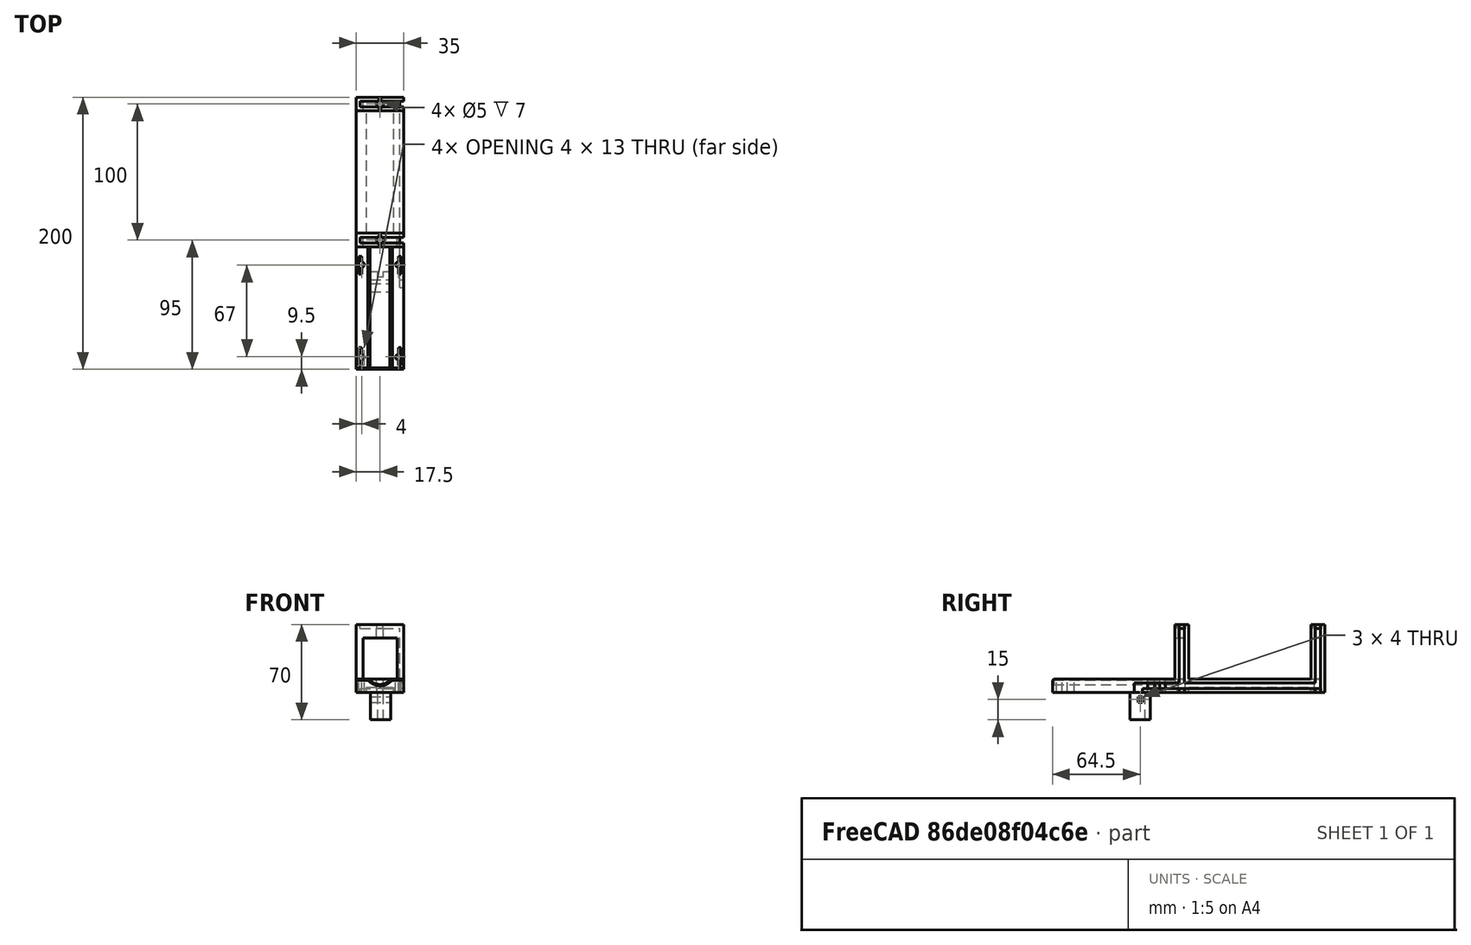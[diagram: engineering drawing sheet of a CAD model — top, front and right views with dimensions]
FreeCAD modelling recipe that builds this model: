
FCSTD DOCUMENT  (FreeCAD 0.19RUnknown)
Label: montaje_02
License: All rights reserved
LicenseURL: http://en.wikipedia.org/wiki/All_rights_reserved
objects: Part::Cut×38, Part::Box×20, Part::Cylinder×11, Part::Chamfer×1, Part::MultiFuse×1
note: 71 computed .brp shape members not serialized (recipe doc carries the construction recipe); baked Part::Feature solids carry a one-line shape summary decoded from their .brp

FEATURE [Part::Box] Box  label="Cubo"
  AttacherType = Attacher::AttachEngine3D
  Height = 10
  Length = 35
  Width = 200
FEATURE [Part::Box] Box001  label="Cubo001"
  AttacherType = Attacher::AttachEngine3D
  Height = 50
  Length = 35
  Placement = pos=(0,90,0) rot=(0,0,1;0rad)
  Width = 10
FEATURE [Part::Box] Box002  label="Cubo002"
  AttacherType = Attacher::AttachEngine3D
  Height = 50
  Length = 35
  Placement = pos=(0,190,0) rot=(0,0,1;0rad)
  Width = 10
FEATURE [Part::Cylinder] Cylinder  label="Cilindro"
  Angle = 360
  AttacherType = Attacher::AttachEngine3D
  Height = 90
  Placement = pos=(17.5,0,16) rot=(-1,0,0;1.5708rad)
  Radius = 10
FEATURE [Part::Cut] Cut
  Base = -> Box
  Tool = -> Cylinder
FEATURE [Part::Chamfer] Chamfer
  Base = -> Cut
  Edges = 5 edges r=1: [Edge6,Edge7,Edge8,Edge12,Edge14]
FEATURE [Part::Box] Box003  label="Cubo003"
  AttacherType = Attacher::AttachEngine3D
  Height = 30
  Length = 25
  Placement = pos=(5,0,10) rot=(0,0,1;0rad)
  Width = 220
FEATURE [Part::Cut] Cut001
  Base = -> Box001
  Tool = -> Box003
FEATURE [Part::Cut] Cut002
  Base = -> Box002
  Tool = -> Box003
FEATURE [Part::Box] Box004  label="Cubo004"
  AttacherType = Attacher::AttachEngine3D
  Height = 4
  Length = 3
  Placement = pos=(32,60,3) rot=(0,0,1;0rad)
  Width = 136
FEATURE [Part::Cut] Cut003
  Base = -> Chamfer
  Tool = -> Box004
FEATURE [Part::Cut] Cut004
  Base = -> Cut001
  Tool = -> Box004
FEATURE [Part::Cut] Cut005
  Base = -> Cut002
  Tool = -> Box004
FEATURE [Part::Box] Box005  label="Cubo005"
  AttacherType = Attacher::AttachEngine3D
  Height = 50
  Length = 3
  Placement = pos=(32,93,0) rot=(0,0,1;0rad)
  Width = 4
FEATURE [Part::Box] Box006  label="Cubo006"
  AttacherType = Attacher::AttachEngine3D
  Height = 50
  Length = 3
  Placement = pos=(32,193,0) rot=(0,0,1;0rad)
  Width = 4
FEATURE [Part::Cut] Cut006
  Base = -> Cut004
  Tool = -> Box005
FEATURE [Part::Cut] Cut007
  Base = -> Cut005
  Tool = -> Box006
FEATURE [Part::Cut] Cut008
  Base = -> Cut003
  Tool = -> Box005
FEATURE [Part::Cut] Cut009
  Base = -> Cut008
  Tool = -> Box006
FEATURE [Part::Box] Box007  label="Cubo007"
  AttacherType = Attacher::AttachEngine3D
  Height = 3
  Length = 30
  Placement = pos=(3,93,0) rot=(0,0,1;0rad)
  Width = 4
FEATURE [Part::Box] Box008  label="Cubo008"
  AttacherType = Attacher::AttachEngine3D
  Height = 3
  Length = 30
  Placement = pos=(3,193,0) rot=(0,0,1;0rad)
  Width = 4
FEATURE [Part::Cut] Cut010
  Base = -> Cut006
  Tool = -> Box007
FEATURE [Part::Cut] Cut011
  Base = -> Cut007
  Tool = -> Box008
FEATURE [Part::Cut] Cut012
  Base = -> Cut009
  Tool = -> Box007
FEATURE [Part::Cut] Cut013
  Base = -> Cut012
  Tool = -> Box008
FEATURE [Part::Box] Box009  label="Cubo009"
  AttacherType = Attacher::AttachEngine3D
  Height = 3
  Length = 30
  Placement = pos=(3,93,47) rot=(0,0,1;0rad)
  Width = 4
FEATURE [Part::Box] Box010  label="Cubo010"
  AttacherType = Attacher::AttachEngine3D
  Height = 3
  Length = 30
  Placement = pos=(3,193,47) rot=(0,0,1;0rad)
  Width = 4
FEATURE [Part::Cut] Cut014
  Base = -> Cut010
  Tool = -> Box009
FEATURE [Part::Cut] Cut015
  Base = -> Cut011
  Tool = -> Box010
FEATURE [Part::Cylinder] Cylinder001  label="Cilindro001"
  Angle = 360
  AttacherType = Attacher::AttachEngine3D
  Height = 60
  Placement = pos=(17.5,95,-1) rot=(0,0,1;0rad)
  Radius = 2.5
FEATURE [Part::Cylinder] Cylinder002  label="Cilindro002"
  Angle = 360
  AttacherType = Attacher::AttachEngine3D
  Height = 60
  Placement = pos=(17.5,195,-1) rot=(0,0,1;0rad)
  Radius = 2.5
FEATURE [Part::Cut] Cut016
  Base = -> Cut014
  Tool = -> Cylinder001
FEATURE [Part::Cut] Cut017
  Base = -> Cut015
  Tool = -> Cylinder002
FEATURE [Part::Cut] Cut018
  Base = -> Cut013
  Tool = -> Cylinder001
FEATURE [Part::Cut] Cut019
  Base = -> Cut018
  Tool = -> Cylinder002
FEATURE [Part::Cylinder] Cylinder003  label="Cilindro003"
  Angle = 360
  AttacherType = Attacher::AttachEngine3D
  Height = 3
  Placement = pos=(17.5,95,0) rot=(0,0,1;0rad)
  Radius = 3
FEATURE [Part::Cylinder] Cylinder004  label="Cilindro004"
  Angle = 360
  AttacherType = Attacher::AttachEngine3D
  Height = 3
  Placement = pos=(17.5,95,47) rot=(0,0,1;0rad)
  Radius = 3
FEATURE [Part::Cylinder] Cylinder005  label="Cilindro005"
  Angle = 360
  AttacherType = Attacher::AttachEngine3D
  Height = 3
  Placement = pos=(17.5,195,0) rot=(0,0,1;0rad)
  Radius = 3
FEATURE [Part::Cylinder] Cylinder006  label="Cilindro006"
  Angle = 360
  AttacherType = Attacher::AttachEngine3D
  Height = 3
  Placement = pos=(17.5,195,47) rot=(0,0,1;0rad)
  Radius = 3
FEATURE [Part::Cut] Cut020
  Base = -> Cut016
  Tool = -> Cylinder004
FEATURE [Part::Cut] Cut021
  Base = -> Cut017
  Tool = -> Cylinder006
FEATURE [Part::Cut] Cut022
  Base = -> Cut020
  Tool = -> Cylinder003
FEATURE [Part::Cut] Cut023
  Base = -> Cut021
  Tool = -> Cylinder005
FEATURE [Part::Cut] Cut024
  Base = -> Cut019
  Tool = -> Cylinder003
FEATURE [Part::Cut] Cut025
  Base = -> Cut024
  Tool = -> Cylinder005
FEATURE [Part::Box] Box014  label="Cubo014"
  AttacherType = Attacher::AttachEngine3D
  Height = 10
  Length = 2
  Placement = pos=(2,3,0) rot=(0,0,1;0rad)
  Width = 13
FEATURE [Part::Box] Box015  label="Cubo015"
  AttacherType = Attacher::AttachEngine3D
  Height = 10
  Length = 2
  Placement = pos=(31,3,0) rot=(0,0,1;0rad)
  Width = 13
FEATURE [Part::Box] Box016  label="Cubo016"
  AttacherType = Attacher::AttachEngine3D
  Height = 10
  Length = 2
  Placement = pos=(2,70,0) rot=(0,0,1;0rad)
  Width = 13
FEATURE [Part::Box] Box017  label="Cubo017"
  AttacherType = Attacher::AttachEngine3D
  Height = 10
  Length = 2
  Placement = pos=(31,70,0) rot=(0,0,1;0rad)
  Width = 13
FEATURE [Part::Cut] Cut028
  Base = -> Cut025
  Tool = -> Box014
FEATURE [Part::Cut] Cut029
  Base = -> Cut028
  Tool = -> Box017
FEATURE [Part::Cut] Cut030
  Base = -> Cut029
  Tool = -> Box016
FEATURE [Part::Cut] Cut031
  Base = -> Cut030
  Tool = -> Box015
FEATURE [Part::Cylinder] Cylinder007  label="Cilindro007"
  Angle = 360
  AttacherType = Attacher::AttachEngine3D
  Height = 10
  Placement = pos=(4,9,0) rot=(0,0,1;0rad)
  Radius = 2
FEATURE [Part::Cylinder] Cylinder008  label="Cilindro008"
  Angle = 360
  AttacherType = Attacher::AttachEngine3D
  Height = 10
  Placement = pos=(31,9,0) rot=(0,0,1;0rad)
  Radius = 2
FEATURE [Part::Cylinder] Cylinder009  label="Cilindro009"
  Angle = 360
  AttacherType = Attacher::AttachEngine3D
  Height = 10
  Placement = pos=(31,77,0) rot=(0,0,1;0rad)
  Radius = 2
FEATURE [Part::Cylinder] Cylinder010  label="Cilindro010"
  Angle = 360
  AttacherType = Attacher::AttachEngine3D
  Height = 10
  Placement = pos=(4,77,0) rot=(0,0,1;0rad)
  Radius = 2
FEATURE [Part::Cut] Cut032
  Base = -> Cut031
  Tool = -> Cylinder007
FEATURE [Part::Cut] Cut033
  Base = -> Cut032
  Tool = -> Cylinder010
FEATURE [Part::Cut] Cut034
  Base = -> Cut033
  Tool = -> Cylinder009
FEATURE [Part::Cut] Cut035
  Base = -> Cut034
  Tool = -> Cylinder008
FEATURE [Part::Box] Box018  label="Cubo018"
  AttacherType = Attacher::AttachEngine3D
  Height = 4
  Length = 20
  Placement = pos=(7.5,100,0) rot=(0,0,1;0rad)
  Width = 90
FEATURE [Part::Cut] Cut036
  Base = -> Cut035
  Refine = true
  Tool = -> Box018
FEATURE [Part::Box] Box019  label="Cubo019"
  AttacherType = Attacher::AttachEngine3D
  Height = 20
  Length = 15
  Placement = pos=(10.5,50,-20) rot=(0,0,1;0rad)
  Width = 15
FEATURE [Part::Box] Box021  label="Cubo021"
  AttacherType = Attacher::AttachEngine3D
  Height = 4
  Length = 3
  Placement = pos=(32,60,0) rot=(0,0,1;0rad)
  Width = 6
FEATURE [Part::Cut] Cut037
  Base = -> Cut036
  Refine = true
  Tool = -> Box021
FEATURE [Part::Box] Box022  label="Cubo022"
  AttacherType = Attacher::AttachEngine3D
  Height = 4
  Length = 20
  Placement = pos=(8,56,-7) rot=(0,0,1;0rad)
  Width = 3
FEATURE [Part::Cut] Cut038
  Base = -> Box019
  Tool = -> Box022
FEATURE [Part::Box] Box023  label="Cubo023"
  AttacherType = Attacher::AttachEngine3D
  Height = 20
  Length = 4
  Placement = pos=(16,61,-20) rot=(0,0,1;0rad)
  Width = 4
FEATURE [Part::Cut] Cut039
  Base = -> Cut038
  Placement = pos=(0,7,0) rot=(0,0,1;0rad)
  Tool = -> Box023
FEATURE [Part::MultiFuse] Fusion
  Shapes = -> [Cut022,Cut023,Cut037,Cut039]
